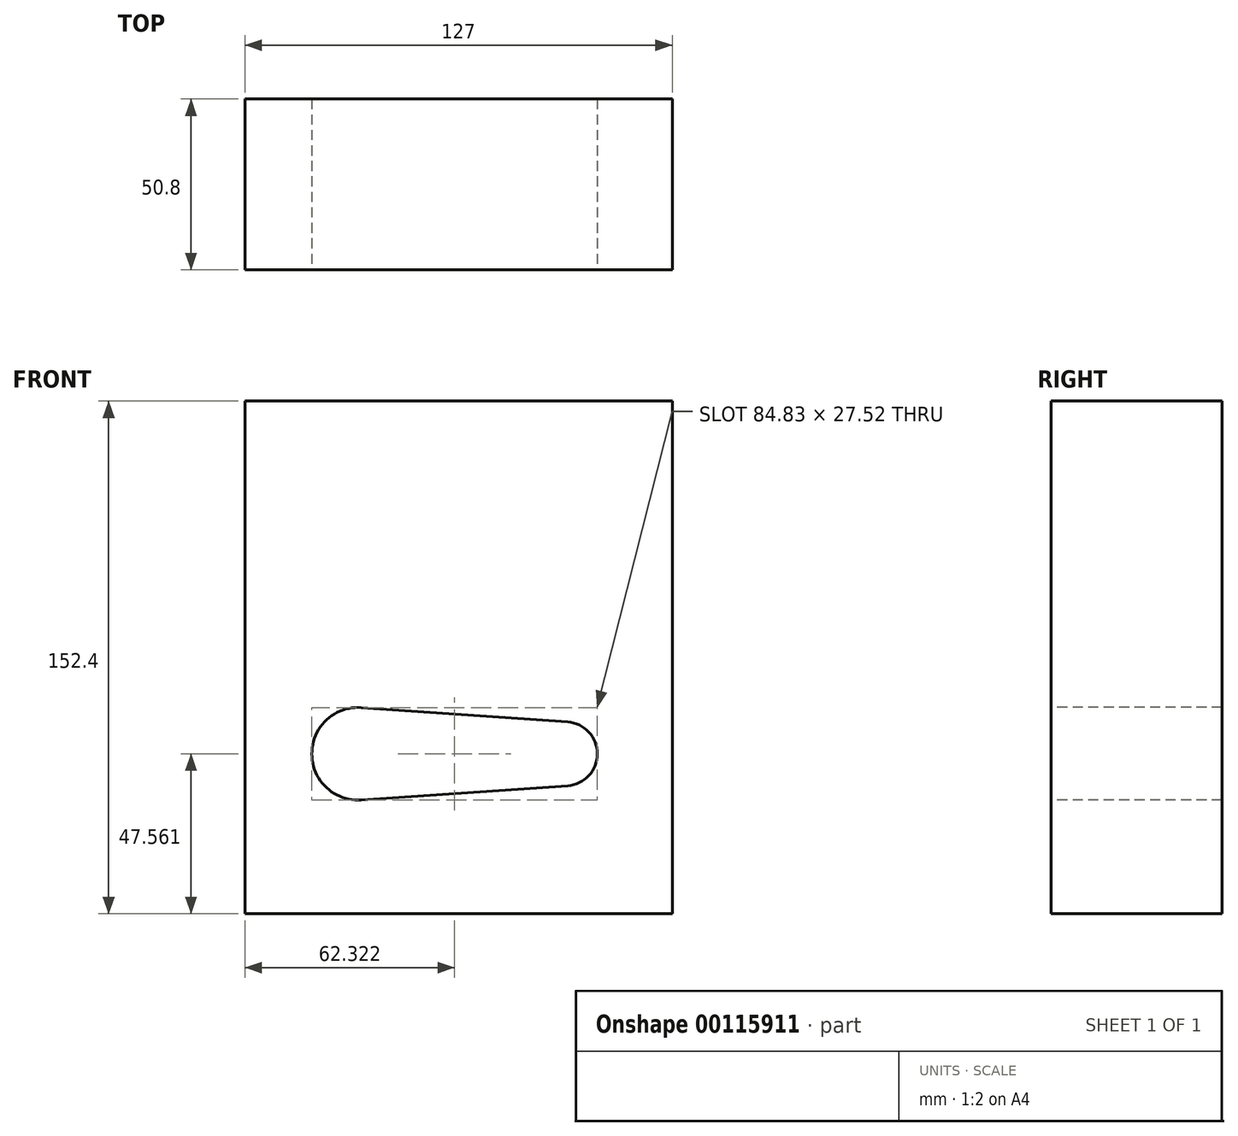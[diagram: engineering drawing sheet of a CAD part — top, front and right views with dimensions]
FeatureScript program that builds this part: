
annotation { "Feature Type Name" : "Feature", "Feature Type Description" : "" }
export const myFeature = defineFeature(function(context is Context, id is Id, definition is map)
    precondition{}
    {
        {
            var Q0;
            Q0=qCreatedBy(makeId("Front.planeOp"),FACE);
            var sketch = newSketch(context, id + "F0", { "sketchPlane" : qUnion([Q0])});
            skLineSegment(sketch, "E0.bottom", {"start": v(0, 0) * mm, "end": v(127, 0) * mm});
            skLineSegment(sketch, "E0.top", {"start": v(0, 152.4) * mm, "end": v(127, 152.4) * mm});
            skLineSegment(sketch, "E0.left", {"start": v(0, 0) * mm, "end": v(0, 152.4) * mm});
            skLineSegment(sketch, "E0.right", {"start": v(127, 0) * mm, "end": v(127, 152.4) * mm});
            skSolve(sketch);
        }
        {
            var Q0;
            Q0=makeQuery(id+"F0.imprint","IMPRINT",FACE,{"disambiguationData":[TD([[makeQuery(id+"F0.imprint","IMPRINT",EDGE,{"derivedFrom":sQuery(id+"F0.wireOp",EDGE,"E0.bottom")}),1.0]])]});
            extrude(context, id + "F1", {"entities" : qUnion([Q0]), "depth" : 25.4 * mm, "hasSecondDirection" : true, "secondDirectionOppositeDirection" : true, "secondDirectionDepth" : 25.4 * mm});
        }
        {
            var Q0;
            Q0=makeQuery(id+"F1.opExtrude","CAP_FACE",FACE,{"disambiguationData":[OSD([sQuery(id+"F0.wireOp",EDGE,"E0.bottom"),sQuery(id+"F0.wireOp",EDGE,"E0.top"),sQuery(id+"F0.wireOp",EDGE,"E0.left"),sQuery(id+"F0.wireOp",EDGE,"E0.right")])],"isStart":false});
            var sketch = newSketch(context, id + "F2", { "sketchPlane" : qUnion([Q0])});
            skArc(sketch, "E1", {"start": v(95.88, 38.07) * mm, "mid": v(104.74, 47.56) * mm, "end": v(95.88, 57.05) * mm});
            skArc(sketch, "E2", {"start": v(34.66, 61.32) * mm, "mid": v(19.9, 47.56) * mm, "end": v(34.66, 33.8) * mm});
            skLineSegment(sketch, "E3", {"start": v(34.66, 61.32) * mm, "end": v(95.88, 57.05) * mm});
            skLineSegment(sketch, "E4", {"start": v(95.88, 38.07) * mm, "end": v(34.66, 33.8) * mm});
            skSolve(sketch);
        }
        {
            var Q0;
            Q0 = qSketchRegion(id + "F2", true);
            extrude(context, id + "F3", {"entities" : qUnion([Q0]), "operationType" : NewBodyOperationType.REMOVE, "endBound" : BoundingType.THROUGH_ALL, "oppositeDirection" : true, "depth" : 25.4 * mm});
        }
    });
